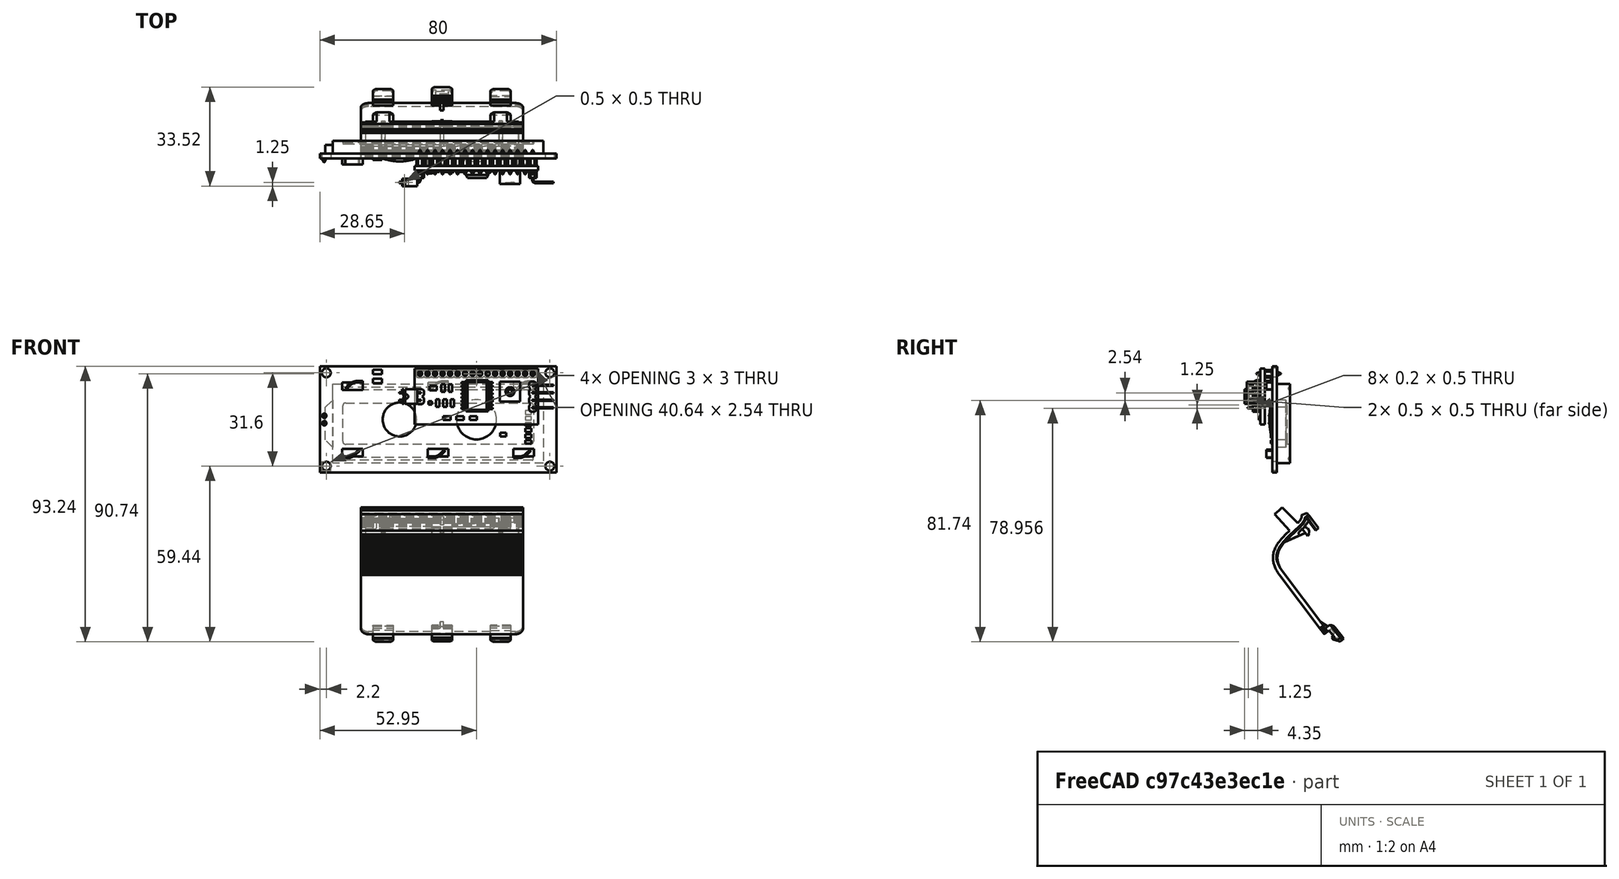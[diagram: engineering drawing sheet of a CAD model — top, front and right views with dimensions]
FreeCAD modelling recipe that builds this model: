
FCSTD DOCUMENT  (FreeCAD 1.0R39109 (Git))
Label: ControllerCAD
License: All rights reserved
LicenseURL: https://en.wikipedia.org/wiki/All_rights_reserved
objects: Part::Feature×5, Part::Scale×4, PartDesign::Pad×3, Mesh::Feature×2, Part::Refine×2, PartDesign::FeatureBase×1, PartDesign::Body×1
note: 23 computed .brp shape members not serialized (recipe doc carries the construction recipe); baked Part::Feature solids carry a one-line shape summary decoded from their .brp

FEATURE [Mesh::Feature] Xbox_One_Controller_Battery_Cover___Standard  label="Xbox_One_Controller_Battery_Cover_-_Standard"
FEATURE [Part::Feature] Xbox_One_Controller_Battery_Cover___Standard001
  shape: bbox 2.188 x 0.8 x 1.676 mm, 2705 faces, 0 solids (baked)
FEATURE [Part::Feature] Xbox_One_Controller_Battery_Cover___Standard001_solid  label="Xbox_One_Controller_Battery_Cover___Standard001 (Solid)"
  shape: bbox 2.188 x 0.8 x 1.676 mm, 2705 faces (baked)
FEATURE [Part::Refine] Xbox_One_Controller_Battery_Cover___Standard001_solid001  label="Xbox_One_Controller_Battery_Cover___Standard001 (Solid)001"
  Source = -> Xbox_One_Controller_Battery_Cover___Standard001_solid
FEATURE [Mesh::Feature] LCD_1602_front  label="LCD-1602_front"
  Placement = pos=(-1,21,63) rot=(1,0,0;3.14159rad)
FEATURE [Part::Feature] Part__Feature  label="LCD_I2C_1602"
  Placement = pos=(-1,12,73) rot=(0,1,0;3.14159rad)
  shape: bbox 80 x 15.35 x 36 mm, 848 faces (baked)
FEATURE [Part::Feature] ImageToStl_com_white_xbox_controller001
  shape: large baked B-rep (31 MB .brp); summary skipped
FEATURE [Part::Feature] LCD_1602_front001
  shape: bbox 119 x 10 x 55 mm, 5642 faces, 0 solids (baked)
FEATURE [Part::Refine] LCD_1602_front002
  Placement = pos=(0,0,10) rot=(0,0,1;0rad)
  Source = -> LCD_1602_front001
FEATURE [Part::Scale] Scale006
  Base = -> ImageToStl_com_white_xbox_controller001
  Uniform = true
  UniformScale = 200
  XScale = 1
  YScale = 1
  ZScale = 1
FEATURE [Part::Scale] Scale008  label="controller"
  Base = -> Scale006
  Placement = pos=(2.21e-14,-38.0128,39.8446) rot=(0,-0.258819,-0.965926;3.14159rad)
  Uniform = true
  UniformScale = 0.93
  XScale = 1
  YScale = 1
  ZScale = 1
FEATURE [PartDesign::FeatureBase] BaseFeature
  BaseFeature = -> Xbox_One_Controller_Battery_Cover___Standard001_solid001
  Suppressed = false
FEATURE [PartDesign::Pad] Pad
  BaseFeature = -> BaseFeature
  Direction = (0,-0.0889821,0.996033)
  Length = 0.3
  Length2 = 10
  Profile = -> BaseFeature [Face501]
  Refine = true
  Suppressed = false
  Type = 0
FEATURE [PartDesign::Pad] Pad001
  BaseFeature = -> Pad
  Direction = (0,-0.111645,0.993748)
  Length = 0.3
  Length2 = 10
  Profile = -> Pad [Face382]
  Refine = true
  Suppressed = false
  Type = 0
FEATURE [PartDesign::Pad] Pad002
  BaseFeature = -> Pad001
  Direction = (0,-0.14818,0.98896)
  Length = 0.3
  Length2 = 10
  Profile = -> Pad001 [Face87]
  Refine = true
  Suppressed = false
  Type = 0
FEATURE [PartDesign::Body] Body
  AllowCompound = false
  BaseFeature = -> Xbox_One_Controller_Battery_Cover___Standard001_solid001
  Group = -> [BaseFeature,Pad,Pad001,Pad002]
  Origin = -> Origin
  Tip = -> Pad002
FEATURE [Part::Scale] Scale  label="battery cover"
  Base = -> Body
  Placement = pos=(270,0,46) rot=(0,0,1;0rad)
  Uniform = true
  UniformScale = 25.34
  XScale = 1
  YScale = 1
  ZScale = 1
FEATURE [Part::Scale] Scale009
  Base = -> Scale
  Placement = pos=(3,29.2689,0.701) rot=(1,0,0;0.645772rad)
  Uniform = true
  UniformScale = 0.99
  XScale = 1
  YScale = 1
  ZScale = 1
